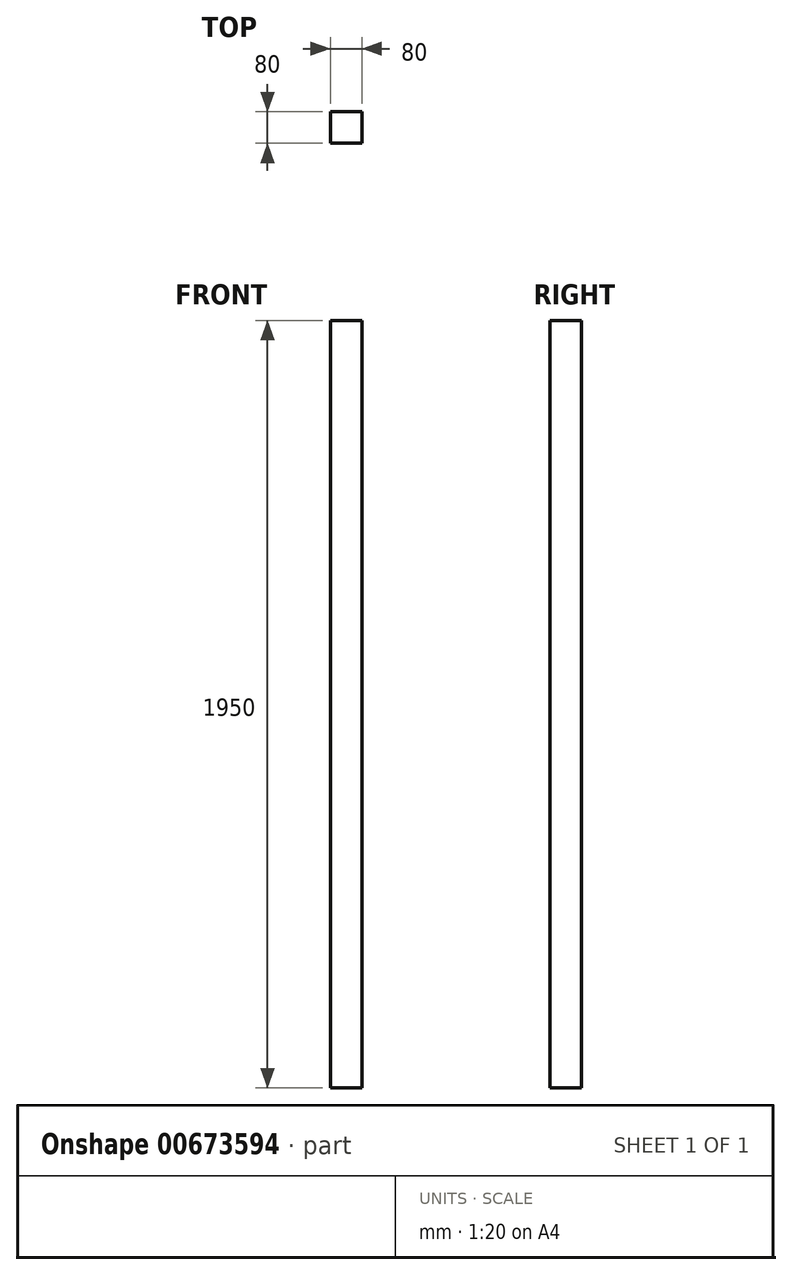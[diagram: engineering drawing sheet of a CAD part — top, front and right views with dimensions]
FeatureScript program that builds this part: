
annotation { "Feature Type Name" : "Feature", "Feature Type Description" : "" }
export const myFeature = defineFeature(function(context is Context, id is Id, definition is map)
    precondition{}
    {
        {
            var Q0;
            Q0=qCreatedBy(makeId("Top.planeOp"),FACE);
            var sketch = newSketch(context, id + "F0", { "sketchPlane" : qUnion([Q0])});
            skLineSegment(sketch, "E0.bottom", {"start": v(40, -40) * mm, "end": v(-40, -40) * mm});
            skLineSegment(sketch, "E0.top", {"start": v(40, 40) * mm, "end": v(-40, 40) * mm});
            skLineSegment(sketch, "E0.left", {"start": v(40, -40) * mm, "end": v(40, 40) * mm});
            skLineSegment(sketch, "E0.right", {"start": v(-40, -40) * mm, "end": v(-40, 40) * mm});
            skPoint(sketch, "E0.middle", {"position": v(0, 0) * mm});
            skSolve(sketch);
        }
        {
            var Q0;
            Q0=makeQuery(id+"F0.imprint","IMPRINT",FACE,{"disambiguationData":[TD([[makeQuery(id+"F0.imprint","IMPRINT",EDGE,{"derivedFrom":sQuery(id+"F0.wireOp",EDGE,"E0.bottom")}),-1.0]])]});
            extrude(context, id + "F1", {"entities" : qUnion([Q0]), "depth" : 1950 * mm, "offsetDistance" : 25 * mm});
        }
    });
